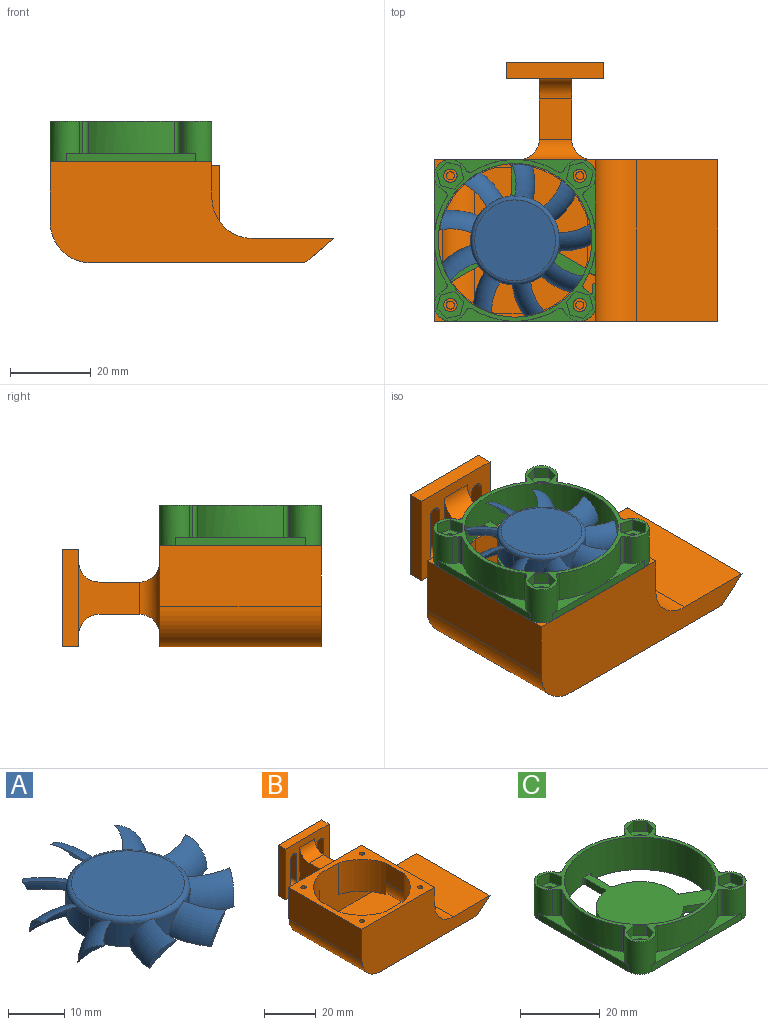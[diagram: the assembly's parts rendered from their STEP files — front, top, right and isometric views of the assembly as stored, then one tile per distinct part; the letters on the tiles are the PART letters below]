
ASSEMBLY  parts=3 mates=1
PART A: 32 faces, bbox 42.3x42.5x6 mm
  f0: cylinder r=11mm len=22mm, axis (0,0,-1), area 307.6mm2, adj f1,f3,f4,f5,f6,f8,f9,f11
  f1: cylinder r=11mm len=4.52mm, axis (0,0,-1), area 3.9mm2, adj f0,f4,f11
  f2: plane 20x20mm, normal (0,0,1), area 314.2mm2, adj f4
  f3: plane 22x22mm, normal (0,0,-1), area 380.1mm2, adj f0
  f4: torus R=10mm, axis (0,0,1), area 102.2mm2, adj f0,f1,f2,f5,f6,f8,f9,f11
  f5: torus R=12.73mm, axis (0,0,-1), area 60.3mm2, adj f0,f4,f6,f7
  f6: torus R=5.4mm, axis (0,0,-1), area 55.4mm2, adj f0,f4,f5,f7
  f7: cylinder r=18.8mm len=4.97mm, axis (0,0,1), area 4.5mm2, adj f5,f6
  f8: torus R=12.73mm, axis (0,0,-1), area 60.3mm2, adj f0,f4,f9,f10
  f9: torus R=5.4mm, axis (0,0,-1), area 55.4mm2, adj f0,f4,f8,f10
  f10: cylinder r=18.8mm len=4.97mm, axis (0,0,1), area 4.5mm2, adj f8,f9
  f11: torus R=12.73mm, axis (0,0,-1), area 60.3mm2, adj f0,f1,f4,f12,f13
  f12: torus R=5.4mm, axis (0,0,-1), area 55.4mm2, adj f0,f4,f11,f13
  f13: cylinder r=18.8mm len=4.97mm, axis (0,0,1), area 4.5mm2, adj f11,f12
  f14: torus R=12.73mm, axis (0,0,-1), area 60.3mm2, adj f0,f4,f15,f16
  f15: torus R=5.4mm, axis (0,0,-1), area 55.4mm2, adj f0,f4,f14,f16
  f16: cylinder r=18.8mm len=4.97mm, axis (0,0,1), area 4.5mm2, adj f14,f15
  f17: torus R=12.73mm, axis (0,0,-1), area 60.3mm2, adj f0,f4,f18,f19
  f18: torus R=5.4mm, axis (0,0,-1), area 55.4mm2, adj f0,f4,f17,f19
  f19: cylinder r=18.8mm len=4.97mm, axis (0,0,1), area 4.5mm2, adj f17,f18
  f20: torus R=12.73mm, axis (0,0,-1), area 60.3mm2, adj f0,f4,f21,f22
  f21: torus R=5.4mm, axis (0,0,-1), area 55.4mm2, adj f0,f4,f20,f22
  f22: cylinder r=18.8mm len=4.99mm, axis (0,0,1), area 4.5mm2, adj f20,f21
  f23: torus R=12.73mm, axis (0,0,-1), area 60.3mm2, adj f0,f4,f24,f25
  f24: torus R=5.4mm, axis (0,0,-1), area 55.4mm2, adj f0,f4,f23,f25
  f25: cylinder r=18.8mm len=4.97mm, axis (0,0,1), area 4.5mm2, adj f23,f24
  f26: torus R=12.73mm, axis (0,0,-1), area 60.3mm2, adj f0,f4,f27,f28
  f27: torus R=5.4mm, axis (0,0,-1), area 55.4mm2, adj f0,f4,f26,f28
  f28: cylinder r=18.8mm len=5mm, axis (0,0,1), area 4.5mm2, adj f26,f27
  f29: torus R=12.73mm, axis (0,0,-1), area 60.3mm2, adj f0,f4,f30,f31
  f30: torus R=5.4mm, axis (0,0,-1), area 55.4mm2, adj f0,f4,f29,f31
  f31: cylinder r=18.8mm len=4.97mm, axis (0,0,1), area 4.5mm2, adj f29,f30
PART B: 56 faces, bbox 70.2x64x25 mm
  f0: plane 70.15x25mm, normal (0,1,0), area 835.5mm2, adj f4,f5,f6,f7,f8,f9,f10,f11
  f1: plane 10.14x9mm, normal (-1,0,0), area 91.2mm2, adj f4,f16,f19,f29
  f2: plane 65.77x23mm, normal (0,1,0), area 514.4mm2, adj f4,f8,f13,f14,f15,f16,f25,f27
  f3: plane 15x10.14mm, normal (1,0,0), area 152.1mm2, adj f4,f13,f22,f25
  f4: plane 40x40mm, normal (0,0,1), area 507.8mm2, adj f0,f1,f2,f3,f5,f11,f12,f17
  f5: plane 40x15mm, normal (-1,0,0), area 600mm2, adj f0,f4,f6,f12
  f6: cylinder r=10mm len=40mm, axis (0,1,0), area 628.3mm2, adj f0,f5,f7,f12
  f7: plane 53x40mm, normal (0,0,-1), area 2120mm2, adj f0,f6,f8,f12
  f8: plane 40x7.15mm, normal (0.64,0,-0.77), area 261.4mm2, adj f0,f2,f7,f9,f12,f14,f15,f17
  f9: plane 40x20.15mm, normal (0,0,1), area 806mm2, adj f0,f8,f10,f12
  f10: cylinder r=10mm len=40mm, axis (0,1,0), area 628.3mm2, adj f0,f9,f11,f12
  f11: plane 40x9mm, normal (1,0,0), area 360mm2, adj f0,f4,f10,f12
  f12: plane 70.15x25mm, normal (0,-1,0), area 1159.5mm2, adj f4,f5,f6,f7,f8,f9,f10,f11
  f13: cylinder r=8mm len=36mm, axis (0,-1,0), area 452.4mm2, adj f2,f3,f14,f17,f24,f27
  f14: plane 55.38x36mm, normal (0,0,1), area 1993.8mm2, adj f2,f8,f13,f17
  f15: plane 36x17.77mm, normal (0,0,-1), area 639.6mm2, adj f2,f8,f16,f17
  f16: cylinder r=12mm len=36mm, axis (0,-1,0), area 678.6mm2, adj f1,f2,f15,f17,f18,f28
  f17: plane 65.77x23mm, normal (0,-1,0), area 514.4mm2, adj f4,f8,f13,f14,f15,f16,f18,f19
  f18: plane 12.93x6mm, normal (1,0,0), area 77.6mm2, adj f16,f17,f19,f21
  f19: cylinder r=18.7mm len=15mm, axis (0,0,1), area 286.6mm2, adj f1,f4,f17,f18,f21
  f20: cylinder r=1mm len=15mm, axis (0,0,1), area 94.2mm2, adj f4,f21
  f21: plane 12.93x12.93mm, normal (0,0,-1), area 51mm2, adj f17,f18,f19,f20
  f22: cylinder r=18.7mm len=15mm, axis (0,0,1), area 286.6mm2, adj f3,f4,f17,f24
  f23: cylinder r=1mm len=15mm, axis (0,0,1), area 94.2mm2, adj f4,f24
  f24: plane 12.93x12.93mm, normal (0,0,-1), area 51mm2, adj f13,f17,f22,f23
  f25: cylinder r=18.7mm len=15mm, axis (0,0,1), area 286.6mm2, adj f2,f3,f4,f27
  f26: cylinder r=1mm len=15mm, axis (0,0,1), area 94.2mm2, adj f4,f27
  f27: plane 12.93x12.93mm, normal (0,0,-1), area 51mm2, adj f2,f13,f25,f26
  f28: plane 12.93x6mm, normal (1,0,0), area 77.6mm2, adj f2,f16,f29,f31
  f29: cylinder r=18.7mm len=15mm, axis (0,0,1), area 286.6mm2, adj f1,f2,f4,f28,f31
  f30: cylinder r=1mm len=15mm, axis (0,0,1), area 94.2mm2, adj f4,f31
  f31: plane 12.93x12.93mm, normal (0,0,-1), area 51mm2, adj f2,f28,f29,f30
  f32: plane 18x15mm, normal (1,0,0), area 130.7mm2, adj f33,f35,f36,f40,f54,f55
  f33: plane 10x8mm, normal (0,0,-1), area 80mm2, adj f32,f34,f38,f54
  f34: plane 18x15mm, normal (-1,0,0), area 130.7mm2, adj f33,f35,f39,f40,f54,f55
  f35: plane 10x8mm, normal (0,0,1), area 80mm2, adj f32,f34,f37,f55
  f36: cylinder r=5mm len=18mm, axis (0,0,1), area 91.4mm2, adj f0,f32,f37,f38
  f37: cylinder r=5mm len=18mm, axis (-1,0,0), area 91.4mm2, adj f0,f35,f36,f39
  f38: cylinder r=5mm len=18mm, axis (1,0,0), area 91.4mm2, adj f0,f33,f36,f39
  f39: cylinder r=5mm len=18mm, axis (0,0,-1), area 91.4mm2, adj f0,f34,f37,f38
  f40: plane 24x24mm, normal (0,-1,0), area 335mm2, adj f32,f34,f41,f42,f43,f44,f46,f47
  f41: plane 24x4mm, normal (1,0,0), area 96mm2, adj f40,f42,f44,f45
  f42: plane 24x4mm, normal (0,0,-1), area 96mm2, adj f40,f41,f43,f45
  f43: plane 24x4mm, normal (-1,0,0), area 96mm2, adj f40,f42,f44,f45
  f44: plane 24x4mm, normal (0,0,1), area 96mm2, adj f40,f41,f43,f45
  f45: plane 24x24mm, normal (0,1,0), area 479mm2, adj f41,f42,f43,f44,f46,f47,f48,f49
  f46: plane 11.6x4mm, normal (-1,0,0), area 46.4mm2, adj f40,f45,f47,f48
  f47: cylinder r=1.7mm len=4mm, axis (0,1,0), area 21.4mm2, adj f40,f45,f46,f49
  f48: cylinder r=1.7mm len=4mm, axis (0,1,0), area 21.4mm2, adj f40,f45,f46,f49
  f49: plane 11.6x4mm, normal (1,0,0), area 46.4mm2, adj f40,f45,f47,f48
  f50: plane 11.6x4mm, normal (-1,0,0), area 46.4mm2, adj f40,f45,f51,f53
  f51: cylinder r=1.7mm len=4mm, axis (0,1,0), area 21.4mm2, adj f40,f45,f50,f52
  f52: plane 11.6x4mm, normal (1,0,0), area 46.4mm2, adj f40,f45,f51,f53
  f53: cylinder r=1.7mm len=4mm, axis (0,1,0), area 21.4mm2, adj f40,f45,f50,f52
  f54: cylinder r=5mm len=8mm, axis (1,0,0), area 62.8mm2, adj f32,f33,f34,f40
  f55: cylinder r=5mm len=8mm, axis (-1,0,0), area 62.8mm2, adj f32,f34,f35,f40
PART C: 115 faces, bbox 40x40x10 mm
  f0: plane 10.28x5.94mm, normal (0.5,0.87,0), area 11.9mm2, adj f19,f33,f35,f80,f81,f82
  f1: plane 2x1.78mm, normal (-1,0,0), area 3.6mm2, adj f8,f33,f81,f97
  f2: plane 16x3.21mm, normal (0,0,1), area 18mm2, adj f26,f27,f56,f57,f100
  f3: plane 16x3.21mm, normal (0,0,1), area 18mm2, adj f25,f26,f65,f69,f106
  f4: plane 16x3.21mm, normal (0,0,1), area 18mm2, adj f21,f22,f34,f60,f102
  f5: plane 16x3.21mm, normal (0,0,1), area 18mm2, adj f23,f24,f62,f63,f104
  f6: plane 16x3.21mm, normal (0,0,1), area 18mm2, adj f27,f28,f57,f58,f101
  f7: plane 35.04x31.24mm, normal (0,0,1), area 457.1mm2, adj f12,f13,f14,f15,f16,f17,f18,f30
  f8: plane 5.45x1.07mm, normal (0,0,1), area 3mm2, adj f1,f28,f29,f81,f96,f97
  f9: plane 16x3.21mm, normal (0,0,1), area 18mm2, adj f22,f23,f61,f62,f103
  f10: plane 8.58x1.89mm, normal (0,0,1), area 5.1mm2, adj f20,f21,f34,f76,f89
  f11: plane 16x3.21mm, normal (0,0,1), area 18mm2, adj f24,f25,f64,f65,f105
  f12: plane 7.04x2mm, normal (1,0,0), area 14.1mm2, adj f7,f33,f87,f92
  f13: cylinder r=19mm len=38mm, axis (0,0,1), area 1168mm2, adj f7,f33,f71,f83,f84,f85,f86,f87
  f14: plane 6.22x3.59mm, normal (0.5,0.87,0), area 14.4mm2, adj f7,f33,f88,f95
  f15: plane 6.09x3.52mm, normal (0.5,-0.87,0), area 14.1mm2, adj f7,f33,f84,f90
  f16: cylinder r=11mm len=16.31mm, axis (0,0,1), area 36.9mm2, adj f7,f33,f90,f94
  f17: plane 6.09x3.52mm, normal (-0.5,0.87,0), area 14.1mm2, adj f7,f33,f85,f91
  f18: plane 7.04x2mm, normal (-1,0,0), area 14.1mm2, adj f7,f33,f86,f93
  f19: cylinder r=11mm len=3.9mm, axis (0,0,1), area 4.4mm2, adj f0,f20,f33,f35,f77
  f20: plane 8.8x5.08mm, normal (-0.5,-0.87,0), area 6.1mm2, adj f10,f19,f33,f76,f77,f78,f89
  f21: plane 24.08x2mm, normal (1,0,0), area 48.2mm2, adj f4,f10,f22,f33,f89
  f22: cylinder r=4mm len=10mm, axis (0,0,1), area 124.5mm2, adj f4,f9,f21,f23,f33,f60,f61,f71
  f23: plane 32x2mm, normal (0,1,0), area 64mm2, adj f5,f9,f22,f24,f33
  f24: cylinder r=4mm len=10mm, axis (0,0,1), area 124.5mm2, adj f5,f11,f23,f25,f33,f63,f64,f71
  f25: plane 32x2mm, normal (-1,0,0), area 64mm2, adj f3,f11,f24,f26,f33
  f26: cylinder r=4mm len=10mm, axis (0,0,1), area 124.5mm2, adj f2,f3,f25,f27,f33,f56,f69,f71
  f27: plane 32x2mm, normal (0,-1,0), area 64mm2, adj f2,f6,f26,f28,f33
  f28: cylinder r=4mm len=10mm, axis (0,0,1), area 124.9mm2, adj f6,f8,f27,f29,f33,f58,f59,f71
  f29: plane 4.96x2mm, normal (1,0,0), area 9.9mm2, adj f8,f28,f33,f96
  f30: plane 6.22x3.59mm, normal (-0.5,-0.87,0), area 14.4mm2, adj f7,f33,f83,f94
  f31: cylinder r=11mm len=15.12mm, axis (0,0,1), area 40.3mm2, adj f7,f33,f91,f93
  f32: cylinder r=11mm len=13.49mm, axis (0,0,1), area 36.9mm2, adj f7,f33,f92,f95
  f33: plane 40x40mm, normal (0,0,-1), area 793.4mm2, adj f0,f1,f12,f13,f14,f15,f16,f17
  f34: cylinder r=20mm len=21.25mm, axis (0,0,1), area 180.4mm2, adj f4,f10,f71,f76,f79,f98,f102
  f35: plane 9.49x8.4mm, normal (0,0,-1), area 34.2mm2, adj f0,f19,f77,f79,f80
  f36: plane 3.35x3mm, normal (-0.26,-0.97,0), area 10.4mm2, adj f37,f70,f71,f75
  f37: plane 3.35x3mm, normal (-0.97,-0.26,0), area 10.4mm2, adj f36,f38,f71,f75
  f38: plane 3x2.45mm, normal (-0.71,0.71,0), area 10.4mm2, adj f37,f39,f71,f75
  f39: plane 3.35x3mm, normal (0.26,0.97,0), area 10.4mm2, adj f38,f40,f71,f75
  f40: plane 3.35x3mm, normal (0.97,0.26,0), area 10.4mm2, adj f39,f70,f71,f75
  f41: plane 3x2.45mm, normal (-0.71,0.71,0), area 10.4mm2, adj f42,f66,f71,f73
  f42: plane 3.35x3mm, normal (0.26,0.97,0), area 10.4mm2, adj f41,f43,f71,f73
  f43: plane 3.35x3mm, normal (0.97,0.26,0), area 10.4mm2, adj f42,f44,f71,f73
  f44: plane 3x2.45mm, normal (0.71,-0.71,0), area 10.4mm2, adj f43,f45,f71,f73
  f45: plane 3.35x3mm, normal (-0.26,-0.97,0), area 10.4mm2, adj f44,f66,f71,f73
  f46: plane 3.35x3mm, normal (-0.97,0.26,0), area 10.4mm2, adj f47,f67,f71,f72
  f47: plane 3.35x3mm, normal (-0.26,0.97,0), area 10.4mm2, adj f46,f48,f71,f72
  f48: plane 3x2.45mm, normal (0.71,0.71,0), area 10.4mm2, adj f47,f49,f71,f72
  f49: plane 3.35x3mm, normal (0.97,-0.26,0), area 10.4mm2, adj f48,f50,f71,f72
  f50: plane 3.35x3mm, normal (0.26,-0.97,0), area 10.4mm2, adj f49,f67,f71,f72
  f51: plane 3x2.45mm, normal (-0.71,-0.71,0), area 10.4mm2, adj f52,f68,f71,f74
  f52: plane 3.35x3mm, normal (-0.97,0.26,0), area 10.4mm2, adj f51,f53,f71,f74
  f53: plane 3.35x3mm, normal (-0.26,0.97,0), area 10.4mm2, adj f52,f54,f71,f74
  f54: plane 3x2.45mm, normal (0.71,0.71,0), area 10.4mm2, adj f53,f55,f71,f74
  f55: plane 3.35x3mm, normal (0.97,-0.26,0), area 10.4mm2, adj f54,f68,f71,f74
  f56: plane 8x1.06mm, normal (0.82,-0.57,0), area 10.4mm2, adj f2,f26,f71,f100
  f57: cylinder r=20mm len=21.25mm, axis (0,0,-1), area 179.2mm2, adj f2,f6,f71,f100,f101
  f58: plane 8x1.06mm, normal (-0.82,-0.57,0), area 10.4mm2, adj f6,f28,f71,f101
  f59: plane 8.5x1.06mm, normal (0.57,0.82,0), area 11mm2, adj f28,f71,f80,f98
  f60: plane 8x1.06mm, normal (0.57,-0.82,0), area 10.4mm2, adj f4,f22,f71,f102
  f61: plane 8x1.06mm, normal (-0.82,0.57,0), area 10.4mm2, adj f9,f22,f71,f103
  f62: cylinder r=20mm len=21.25mm, axis (0,0,-1), area 179.2mm2, adj f5,f9,f71,f103,f104
  f63: plane 8x1.06mm, normal (0.82,0.57,0), area 10.4mm2, adj f5,f24,f71,f104
  f64: plane 8x1.06mm, normal (-0.57,-0.82,0), area 10.4mm2, adj f11,f24,f71,f105
  f65: cylinder r=20mm len=21.25mm, axis (0,0,-1), area 179.2mm2, adj f3,f11,f71,f105,f106
  f66: plane 3.35x3mm, normal (-0.97,-0.26,0), area 10.4mm2, adj f41,f45,f71,f73
  f67: plane 3x2.45mm, normal (-0.71,-0.71,0), area 10.4mm2, adj f46,f50,f71,f72
  f68: plane 3.35x3mm, normal (0.26,-0.97,0), area 10.4mm2, adj f51,f55,f71,f74
  f69: plane 8x1.06mm, normal (-0.57,0.82,0), area 10.4mm2, adj f3,f26,f71,f106
  f70: plane 3x2.45mm, normal (0.71,-0.71,0), area 10.4mm2, adj f36,f40,f71,f75
  f71: plane 40x40mm, normal (0,0,1), area 183.3mm2, adj f13,f22,f24,f26,f28,f34,f36,f37
  f72: plane 6.69x6.69mm, normal (0,0,1), area 22.6mm2, adj f46,f47,f48,f49,f50,f67,f111
  f73: plane 6.69x6.69mm, normal (0,0,1), area 22.6mm2, adj f41,f42,f43,f44,f45,f66,f109
  f74: plane 6.69x6.69mm, normal (0,0,1), area 22.6mm2, adj f51,f52,f53,f54,f55,f68,f107
  f75: plane 6.69x6.69mm, normal (0,0,1), area 22.6mm2, adj f36,f37,f38,f39,f40,f70,f113
  f76: cylinder r=0.5mm len=0.7mm, axis (0,0,1), area 0.4mm2, adj f10,f20,f34,f78
  f77: cylinder r=0.5mm len=7.74mm, axis (0.87,-0.5,0), area 6.8mm2, adj f19,f20,f35,f78
  f78: bspline ~1.22x1.19mm, area 0.9mm2, adj f20,f76,f77,f79
  f79: torus R=19.5mm, axis (0,0,1), area 2.5mm2, adj f34,f35,f78,f99
  f80: cylinder r=0.5mm len=2.57mm, axis (0.82,-0.57,0), area 1.5mm2, adj f0,f35,f59,f82,f99
  f81: cylinder r=0.5mm len=2mm, axis (0,0,-1), area 1.7mm2, adj f0,f1,f8,f28,f33,f82
  f82: torus R=3.5mm, axis (0,0,1), area 0.4mm2, adj f0,f28,f80,f81
  f83: cylinder r=0.5mm len=2mm, axis (0,0,1), area 1.7mm2, adj f7,f13,f30,f33
  f84: cylinder r=0.5mm len=2mm, axis (0,0,1), area 1.7mm2, adj f7,f13,f15,f33
  f85: cylinder r=0.5mm len=2mm, axis (0,0,1), area 1.7mm2, adj f7,f13,f17,f33
  f86: cylinder r=0.5mm len=2mm, axis (0,0,1), area 1.7mm2, adj f7,f13,f18,f33
  f87: cylinder r=0.5mm len=2mm, axis (0,0,1), area 1.7mm2, adj f7,f12,f13,f33
  f88: cylinder r=0.5mm len=2mm, axis (0,0,1), area 1.7mm2, adj f7,f13,f14,f33
  f89: cylinder r=0.5mm len=2mm, axis (0,0,-1), area 2.1mm2, adj f10,f20,f21,f33
  f90: cylinder r=0.5mm len=2mm, axis (0,0,1), area 1.4mm2, adj f7,f15,f16,f33
  f91: cylinder r=0.5mm len=2mm, axis (0,0,1), area 1.4mm2, adj f7,f17,f31,f33
  f92: cylinder r=0.5mm len=2mm, axis (0,0,1), area 1.4mm2, adj f7,f12,f32,f33
  f93: cylinder r=0.5mm len=2mm, axis (0,0,1), area 1.4mm2, adj f7,f18,f31,f33
  f94: cylinder r=0.5mm len=2mm, axis (0,0,1), area 1.3mm2, adj f7,f16,f30,f33
  f95: cylinder r=0.5mm len=2mm, axis (0,0,1), area 1.3mm2, adj f7,f14,f32,f33
  f96: cylinder r=0.5mm len=2mm, axis (0,0,1), area 1.4mm2, adj f8,f29,f33,f97
  f97: cylinder r=0.5mm len=2mm, axis (0,0,1), area 1.4mm2, adj f1,f8,f33,f96
  f98: cylinder r=1mm len=8.5mm, axis (0,0,1), area 12.9mm2, adj f34,f59,f71,f99
  f99: bspline ~1.5x1.35mm, area 0.5mm2, adj f79,f80,f98
  f100: cylinder r=1mm len=8mm, axis (0,0,-1), area 12.2mm2, adj f2,f56,f57,f71
  f101: cylinder r=1mm len=8mm, axis (0,0,-1), area 12.2mm2, adj f6,f57,f58,f71
  f102: cylinder r=1mm len=8mm, axis (0,0,1), area 12.2mm2, adj f4,f34,f60,f71
  f103: cylinder r=1mm len=8mm, axis (0,0,-1), area 12.2mm2, adj f9,f61,f62,f71
  f104: cylinder r=1mm len=8mm, axis (0,0,-1), area 12.2mm2, adj f5,f62,f63,f71
  f105: cylinder r=1mm len=8mm, axis (0,0,-1), area 12.2mm2, adj f11,f64,f65,f71
  f106: cylinder r=1mm len=8mm, axis (0,0,-1), area 12.2mm2, adj f3,f65,f69,f71
  f107: cylinder r=1.65mm len=6.4mm, axis (0,0,-1), area 66.4mm2, adj f74,f108
  f108: cone r=1.65mm half-angle=45deg, axis (0,0,-1), area 10.4mm2, adj f33,f107
  f109: cylinder r=1.65mm len=6.4mm, axis (0,0,-1), area 66.4mm2, adj f73,f110
  f110: cone r=1.65mm half-angle=45deg, axis (0,0,-1), area 10.4mm2, adj f33,f109
  f111: cylinder r=1.65mm len=6.4mm, axis (0,0,-1), area 66.4mm2, adj f72,f112
  f112: cone r=1.65mm half-angle=45deg, axis (0,0,-1), area 10.4mm2, adj f33,f111
  f113: cylinder r=1.65mm len=6.4mm, axis (0,0,-1), area 66.4mm2, adj f75,f114
  f114: cone r=1.65mm half-angle=45deg, axis (0,0,-1), area 10.4mm2, adj f33,f113
PLACE A t=(10,-20,17)mm
PLACE B at identity
PLACE C t=(10,-20,17)mm
MATE planar C.f28 <-> B.f30  axis (0,0,-1) through (26,-36,15)mm
